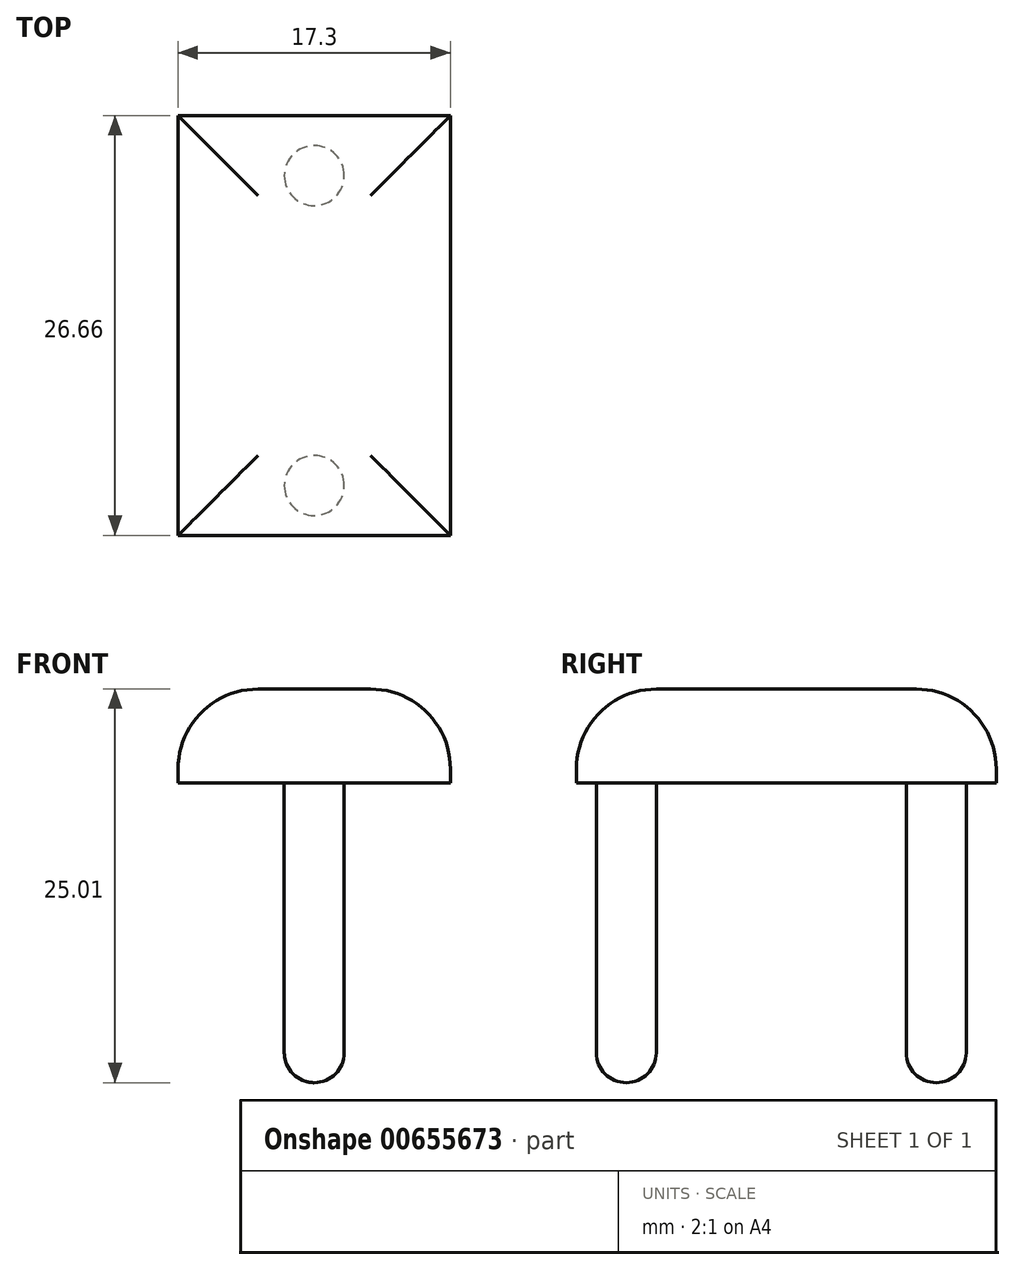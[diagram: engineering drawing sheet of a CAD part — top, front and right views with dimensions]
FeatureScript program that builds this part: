
annotation { "Feature Type Name" : "Feature", "Feature Type Description" : "" }
export const myFeature = defineFeature(function(context is Context, id is Id, definition is map)
    precondition{}
    {
        {
            var Q0;
            Q0=qCreatedBy(makeId("Front.planeOp"),FACE);
            var sketch = newSketch(context, id + "F0", { "sketchPlane" : qUnion([Q0])});
            skLineSegment(sketch, "E0.bottom", {"start": v(8.65, 2.98) * mm, "end": v(-8.65, 2.98) * mm});
            skLineSegment(sketch, "E0.top", {"start": v(8.65, -2.98) * mm, "end": v(-8.65, -2.98) * mm});
            skLineSegment(sketch, "E0.left", {"start": v(8.65, 2.98) * mm, "end": v(8.65, -2.98) * mm});
            skLineSegment(sketch, "E0.right", {"start": v(-8.65, 2.98) * mm, "end": v(-8.65, -2.98) * mm});
            skPoint(sketch, "E0.middle", {"position": v(0, 0) * mm});
            skSolve(sketch);
        }
        {
            var Q0;
            Q0 = qSketchRegion(id + "F0", true);
            extrude(context, id + "F1", {"entities" : qUnion([Q0]), "depth" : 13.33 * mm, "offsetDistance" : 25.4 * mm});
        }
        {
            var Q0;
            Q0 = qSketchRegion(id + "F0", true);
            extrude(context, id + "F2", {"entities" : qUnion([Q0]), "operationType" : NewBodyOperationType.ADD, "oppositeDirection" : true, "depth" : 13.33 * mm, "offsetDistance" : 25.4 * mm});
        }
        {
            var Q0;
            {var subQ0=sQuery(id+"F0.wireOp",EDGE,"E0.left");var subQ1=sQuery(id+"F0.wireOp",EDGE,"E0.bottom");Q0=makeQuery(id+"F2.boolean.opBoolean","MERGE",EDGE,{"derivedFrom":[makeQuery(id+"F1.opExtrude","SWEPT_EDGE",EDGE,{"disambiguationData":[OSD([subQ1,subQ0])]}),makeQuery(id+"F2.opExtrude","SWEPT_EDGE",EDGE,{"disambiguationData":[OSD([subQ1,subQ0])]})]});}
            var Q1;
            Q1=makeQuery(id+"F2.opExtrude","CAP_EDGE",EDGE,{"disambiguationData":[OSD([sQuery(id+"F0.wireOp",EDGE,"E0.bottom")])],"isStart":false});
            var Q2;
            {var subQ0=sQuery(id+"F0.wireOp",EDGE,"E0.right");var subQ1=sQuery(id+"F0.wireOp",EDGE,"E0.bottom");Q2=makeQuery(id+"F2.boolean.opBoolean","MERGE",EDGE,{"derivedFrom":[makeQuery(id+"F1.opExtrude","SWEPT_EDGE",EDGE,{"disambiguationData":[OSD([subQ1,subQ0])]}),makeQuery(id+"F2.opExtrude","SWEPT_EDGE",EDGE,{"disambiguationData":[OSD([subQ1,subQ0])]})]});}
            var Q3;
            Q3=makeQuery(id+"F1.opExtrude","CAP_EDGE",EDGE,{"disambiguationData":[OSD([sQuery(id+"F0.wireOp",EDGE,"E0.bottom")])],"isStart":false});
            fillet(context, id + "F3", {"entities" : qUnion([Q0, Q1, Q2, Q3]), "radius" : 5.08 * mm, "tangentPropagation" : true, "allowEdgeOverflow" : false});
        }
        {
            var Q0;
            {var subQ0=sQuery(id+"F0.wireOp",EDGE,"E0.top");Q0=makeQuery(id+"F2.boolean.opBoolean","MERGE",FACE,{"derivedFrom":[makeQuery(id+"F1.opExtrude","SWEPT_FACE",FACE,{"disambiguationData":[OSD([subQ0])]}),makeQuery(id+"F2.opExtrude","SWEPT_FACE",FACE,{"disambiguationData":[OSD([subQ0])]})]});}
            var sketch = newSketch(context, id + "F4", { "sketchPlane" : qUnion([Q0])});
            skCircle(sketch, "E1", {"center": v(0, 10.16) * mm, "radius": 1.9 * mm});
            skCircle(sketch, "E2", {"center": v(0, -9.52) * mm, "radius": 1.9 * mm});
            skLineSegment(sketch, "E3", {"start": v(-8.65, 0) * mm, "end": v(8.65, 0) * mm, "construction": true});
            skSolve(sketch);
        }
        {
            var Q0;
            Q0=makeQuery(id+"F4.imprint","IMPRINT",FACE,{"disambiguationData":[TD([[makeQuery(id+"F4.imprint","IMPRINT",EDGE,{"derivedFrom":sQuery(id+"F4.wireOp",EDGE,"E1")}),1.0]])]});
            var Q1;
            Q1=makeQuery(id+"F4.imprint","IMPRINT",FACE,{"disambiguationData":[TD([[makeQuery(id+"F4.imprint","IMPRINT",EDGE,{"derivedFrom":sQuery(id+"F4.wireOp",EDGE,"E2")}),1.0]])]});
            extrude(context, id + "F5", {"entities" : qUnion([Q0, Q1]), "operationType" : NewBodyOperationType.ADD, "depth" : 19.05 * mm, "offsetDistance" : 25.4 * mm});
        }
        {
            var Q0;
            Q0=makeQuery(id+"F5.opExtrude","CAP_EDGE",EDGE,{"disambiguationData":[OSD([sQuery(id+"F4.wireOp",EDGE,"E1")])],"isStart":false});
            var Q1;
            Q1=makeQuery(id+"F5.opExtrude","CAP_EDGE",EDGE,{"disambiguationData":[OSD([sQuery(id+"F4.wireOp",EDGE,"E2")])],"isStart":false});
            fillet(context, id + "F6", {"entities" : qUnion([Q0, Q1]), "radius" : 1.9 * mm, "tangentPropagation" : true, "allowEdgeOverflow" : false});
        }
    });
